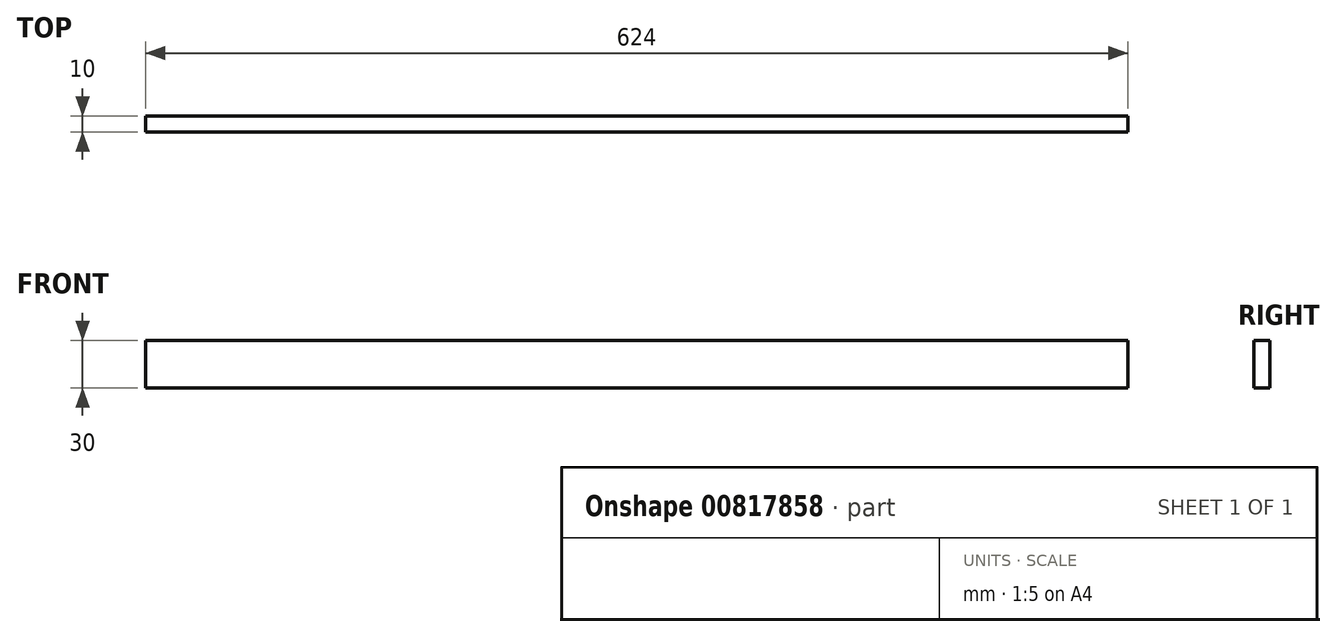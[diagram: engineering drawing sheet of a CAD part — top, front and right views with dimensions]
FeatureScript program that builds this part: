
annotation { "Feature Type Name" : "Feature", "Feature Type Description" : "" }
export const myFeature = defineFeature(function(context is Context, id is Id, definition is map)
    precondition{}
    {
        {
            var Q0;
            Q0=qCreatedBy(makeId("Front.planeOp"),FACE);
            var sketch = newSketch(context, id + "F0", { "sketchPlane" : qUnion([Q0])});
            skLineSegment(sketch, "E0.bottom", {"start": v(0, 0) * mm, "end": v(624, 0) * mm});
            skLineSegment(sketch, "E0.top", {"start": v(0, 30) * mm, "end": v(624, 30) * mm});
            skLineSegment(sketch, "E0.left", {"start": v(0, 0) * mm, "end": v(0, 30) * mm});
            skLineSegment(sketch, "E0.right", {"start": v(624, 0) * mm, "end": v(624, 30) * mm});
            skSolve(sketch);
        }
        {
            var Q0;
            Q0=makeQuery(id+"F0.imprint","IMPRINT",FACE,{"disambiguationData":[TD([[makeQuery(id+"F0.imprint","IMPRINT",EDGE,{"derivedFrom":sQuery(id+"F0.wireOp",EDGE,"E0.bottom")}),1.0]])]});
            extrude(context, id + "F1", {"entities" : qUnion([Q0]), "depth" : 10 * mm, "offsetDistance" : 25 * mm});
        }
    });
